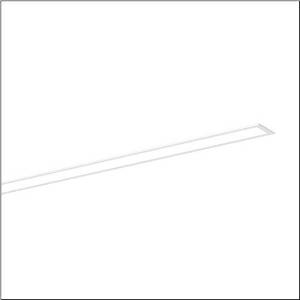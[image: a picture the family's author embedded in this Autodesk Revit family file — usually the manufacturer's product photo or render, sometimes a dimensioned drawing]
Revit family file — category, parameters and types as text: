
# Revit family: silica_21_51mx10da32wb
name_source: partatom
category: Lighting Fixtures
units: mm (PartAtom-declared; Revit-internal decimal feet)

## family parameters
Cut with Voids When Loaded = No
Host = Face
Light Source = No
Part Type = Normal
Room Calculation Point = No
Round Connector Dimension = Use Diameter
Shared = No

## types (1)
- --- (1 x LED, 2400 lm, 16.1 W, 3000K)
    Apparent Load = 16 VA
    CIE Flux Codes = 48 79 96 100 100
    Color Rendering = 80
    Color Temperature = 3000K
    Default Elevation = 1800 mm
    Description = Silica 21, office luminaire, primary optical cover: cover, of PMMA, opal, light emission: direct distribution, primary light characteristic: symmetric, installation type: recessed, LED, rated luminous flux: 2.400lm, luminous efficacy: 149lm/W, light colour: 830, colour temperature: 3000K, control gear: DALI 2, with terminal, 3+2-pole, max. 2.5mm², mains connection: 220..240V, AC, 50/60Hz, rated input power: 16.1W, luminaire housing, of aluminium, traffic white (RAL 9016), length: 1.228mm, width: 79mm, height: 53mm, protection rating (complete): IP20, insulation class (complete): insulation class I (protective earthing), certification: CE, ENEC, VDE, permissible operating ambient temperature: 0..+35°C, standard: EN 50419, packaging unit: 1 piece
    Height = 0 mm  [stored 0 ft]
    Lamp = 1 x LED
    Lamp Light Flux = 2400 lm
    Lamp Power = 16.1 W
    Lamp count = 1
    Length = 1227 mm
    Luminous efficacy = 149 lm/W
    Manufacturer = Siteco
    ModVariant = No
    Model = 51MX10DA32WB
    Mounting Place = Ceiling
    Mounting Type = Recessed
    Number of Poles = 1
    OnlyDefault = Yes
    Power Factor = 1
    Product Name = Silica 21
    Product group = office luminaire | ceiling recessed
    ProductGroupID = 400
    Protection Class = Protection class I
    Protection Degree = IP 20
    RLX_Detail_Level = 1
    RLX_Emergency_Light_Flux = 0 lm
    RLX_Emergency_Type = 0
    RLX_Emergency_Type_DB = No
    RlxData = <blob elided: 21061 chars, md5=0b9b0139>
    Socket = socket
    Standby Power = 0 W
    System Light Flux = 2400 lm
    System Power = 16 W
    Type Comments = factory setting: luminous flux: 100 % | dim-lin: 254 | 233 mA
    Type Image = l_1335891.jpg
    URL = http://relux.com
    VarID = @adj_027673
    Voltage = 0 V
    Weight = 0.00 kg
    Width = 79 mm

note: [stored X ft] marks values corroborated as IEEE doubles in the binary element streams (Revit-internal decimal feet)

## geometry (parser evidence)
native form markers: Blend x4, Sweep x12
no freeform markers — native parametric forms only
